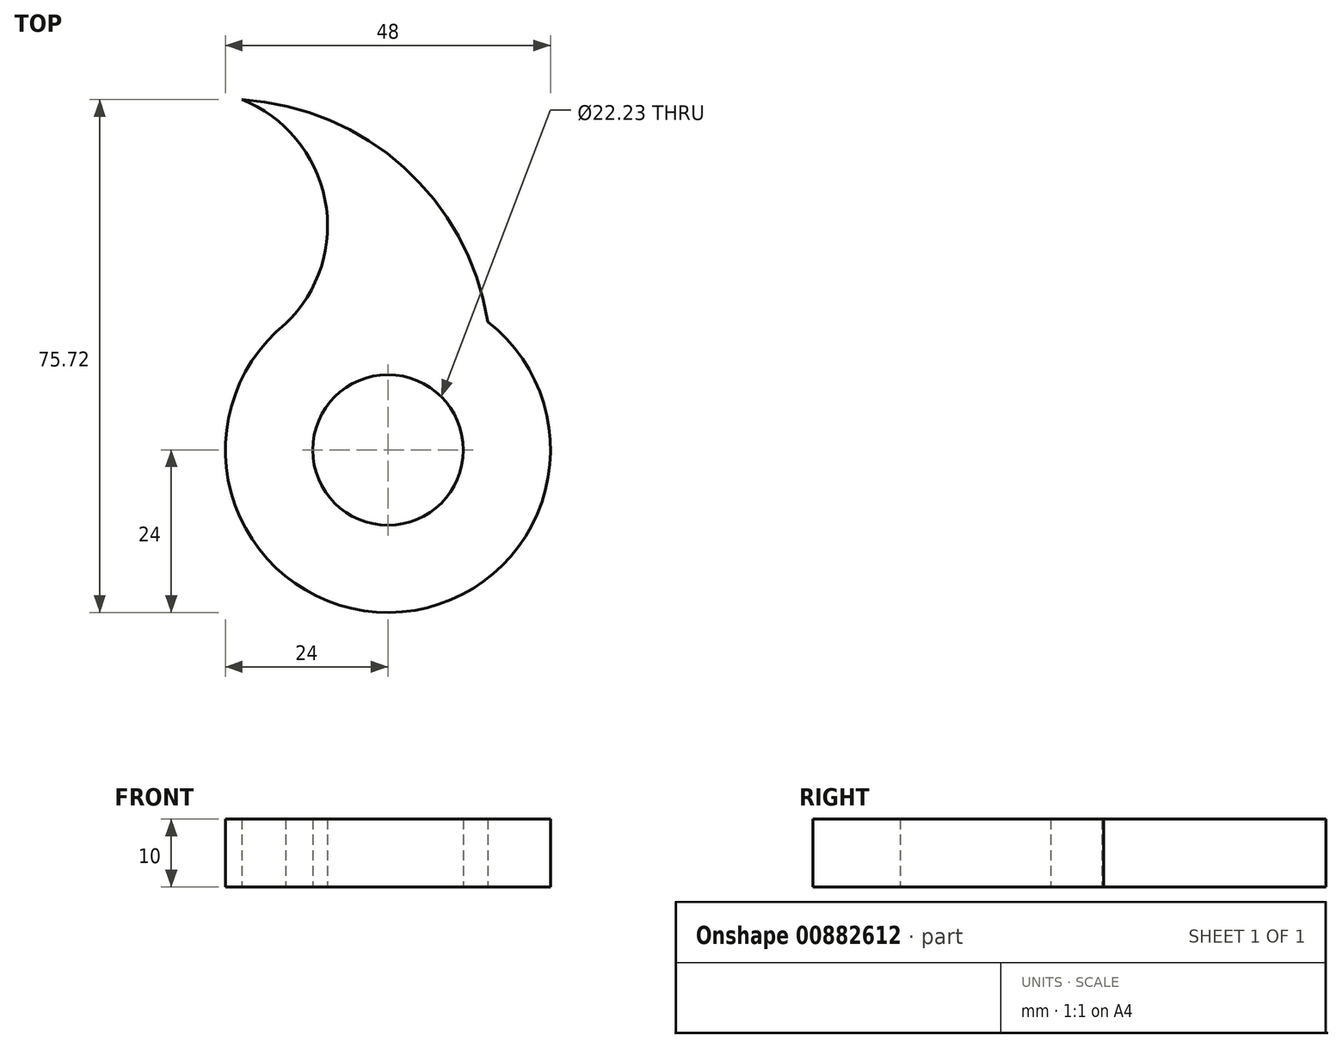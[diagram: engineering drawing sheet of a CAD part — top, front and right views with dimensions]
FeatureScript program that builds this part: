
annotation { "Feature Type Name" : "Feature", "Feature Type Description" : "" }
export const myFeature = defineFeature(function(context is Context, id is Id, definition is map)
    precondition{}
    {
        {
            var Q0;
            Q0=qCreatedBy(makeId("Top.planeOp"),FACE);
            var sketch = newSketch(context, id + "F0", { "sketchPlane" : qUnion([Q0])});
            skCircle(sketch, "E0", {"center": v(0, 0) * mm, "radius": 11.12 * mm});
            skSolve(sketch);
        }
        {
            var Q0;
            Q0=qCreatedBy(makeId("Top.planeOp"),FACE);
            var sketch = newSketch(context, id + "F1", { "sketchPlane" : qUnion([Q0])});
            skCircle(sketch, "E1", {"center": v(0, 0) * mm, "radius": 24 * mm});
            skArc(sketch, "E2", {"start": v(-15.1, 18.65) * mm, "mid": v(-9.3, 36.96) * mm, "end": v(-21.6, 51.72) * mm});
            skArc(sketch, "E3", {"start": v(14.76, 18.92) * mm, "mid": v(2.36, 41.72) * mm, "end": v(-21.6, 51.72) * mm});
            skSolve(sketch);
        }
        {
            var Q0;
            {var subQ0=sQuery(id+"F1.wireOp",EDGE,"E2");Q0=makeQuery(id+"F1.imprint","IMPRINT",FACE,{"disambiguationData":[TD([[makeQuery(id+"F1.imprint","IMPRINT",EDGE,{"derivedFrom":subQ0}),-1.0]])]});}
            var Q1;
            {var subQ0=sQuery(id+"F1.wireOp",EDGE,"E1");var subQ1=makeQuery(id+"F1.imprint","INTERSECT",VERTEX,{"derivedFrom":[subQ0,sQuery(id+"F1.wireOp",EDGE,"E2")]});Q1=makeQuery(id+"F1.imprint","IMPRINT",FACE,{"disambiguationData":[TD([[makeQuery(id+"F1.imprint","IMPRINT",EDGE,{"disambiguationData":[TD([[subQ1,1.0]])],"derivedFrom":subQ0}),1.0]])]});}
            extrude(context, id + "F2", {"entities" : qUnion([Q0, Q1]), "depth" : 10 * mm, "offsetDistance" : 25 * mm});
        }
        {
            var Q0;
            Q0 = qSketchRegion(id + "F0", true);
            extrude(context, id + "F3", {"entities" : qUnion([Q0]), "operationType" : NewBodyOperationType.REMOVE, "endBound" : BoundingType.SYMMETRIC, "depth" : 25 * mm, "offsetDistance" : 25 * mm});
        }
    });
